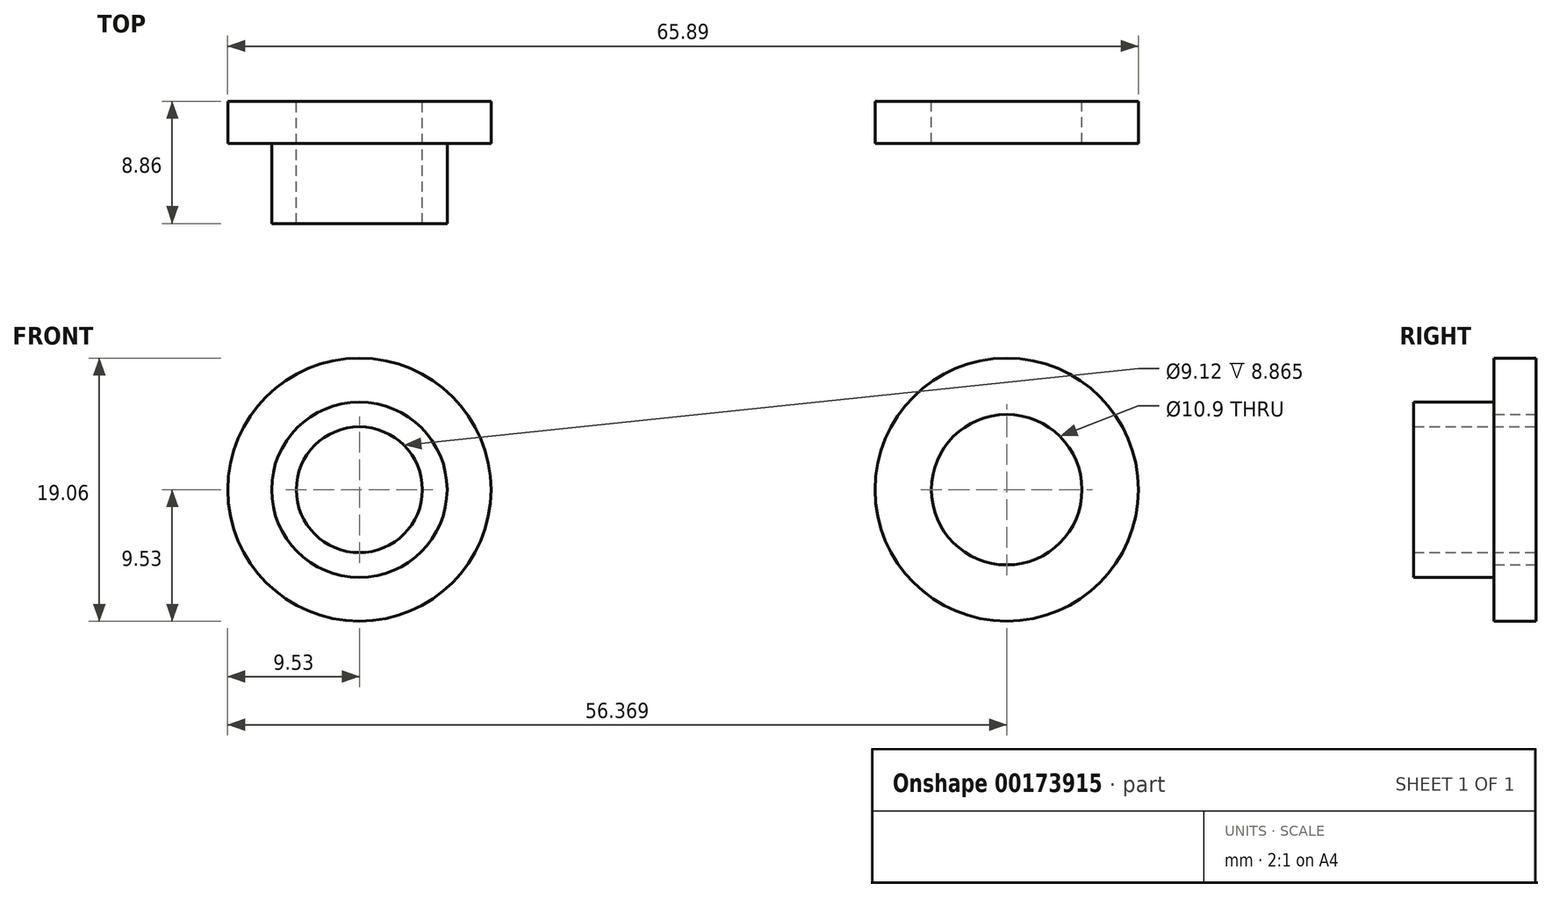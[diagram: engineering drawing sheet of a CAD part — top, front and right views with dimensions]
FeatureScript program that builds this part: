
annotation { "Feature Type Name" : "Feature", "Feature Type Description" : "" }
export const myFeature = defineFeature(function(context is Context, id is Id, definition is map)
    precondition{}
    {
        {
            var Q0;
            Q0=qCreatedBy(makeId("Front.planeOp"),FACE);
            var sketch = newSketch(context, id + "F0", { "sketchPlane" : qUnion([Q0])});
            skCircle(sketch, "E0", {"center": v(0, 0) * mm, "radius": 4.56 * mm});
            skCircle(sketch, "E1", {"center": v(0, 0) * mm, "radius": 6.35 * mm});
            skCircle(sketch, "E2", {"center": v(0, 0) * mm, "radius": 9.53 * mm});
            skCircle(sketch, "E3", {"center": v(46.84, 0) * mm, "radius": 9.53 * mm});
            skCircle(sketch, "E4", {"center": v(46.84, 0) * mm, "radius": 5.45 * mm});
            skSolve(sketch);
        }
        {
            var Q0;
            Q0 = qSketchRegion(id + "F0", true);
            extrude(context, id + "F1", {"entities" : qUnion([Q0]), "depth" : 3.05 * mm});
        }
        {
            var Q0;
            Q0=makeQuery(id+"F0.imprint","IMPRINT",FACE,{"disambiguationData":[TD([[makeQuery(id+"F0.imprint","IMPRINT",EDGE,{"derivedFrom":sQuery(id+"F0.wireOp",EDGE,"E0")}),-1.0]])]});
            extrude(context, id + "F2", {"entities" : qUnion([Q0]), "operationType" : NewBodyOperationType.ADD, "depth" : 8.86 * mm});
        }
    });
